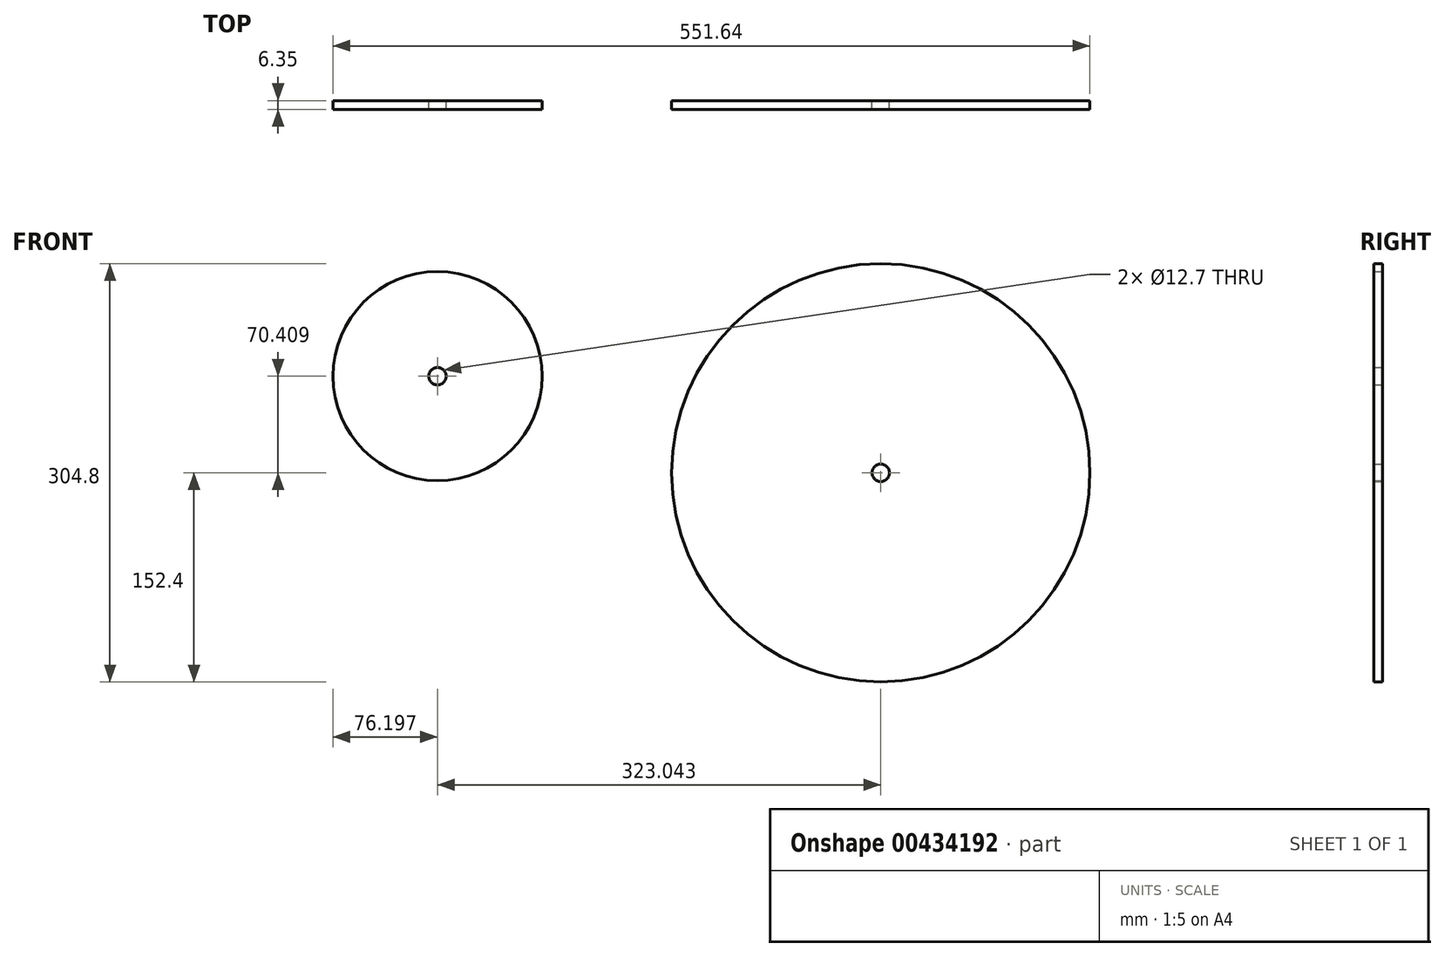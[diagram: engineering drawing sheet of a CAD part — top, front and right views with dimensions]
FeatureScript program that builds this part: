
annotation { "Feature Type Name" : "Feature", "Feature Type Description" : "" }
export const myFeature = defineFeature(function(context is Context, id is Id, definition is map)
    precondition{}
    {
        {
            var Q0;
            Q0=qCreatedBy(makeId("Front.planeOp"),FACE);
            var sketch = newSketch(context, id + "F0", { "sketchPlane" : qUnion([Q0])});
            skCircle(sketch, "E0", {"center": v(0, 0) * mm, "radius": 152.4 * mm});
            skCircle(sketch, "E1", {"center": v(0, 0) * mm, "radius": 6.35 * mm});
            skSolve(sketch);
        }
        {
            var Q0;
            Q0=qCreatedBy(makeId("Front.planeOp"),FACE);
            var sketch = newSketch(context, id + "F1", { "sketchPlane" : qUnion([Q0])});
            skCircle(sketch, "E2", {"center": v(-323.04, 70.4) * mm, "radius": 76.2 * mm});
            skCircle(sketch, "E3", {"center": v(-323.04, 70.4) * mm, "radius": 6.35 * mm});
            skSolve(sketch);
        }
        {
            var Q0;
            Q0 = qSketchRegion(id + "F1", true);
            var Q1;
            Q1 = qSketchRegion(id + "F0", true);
            extrude(context, id + "F2", {"entities" : qUnion([Q0, Q1]), "depth" : 6.35 * mm});
        }
    });
